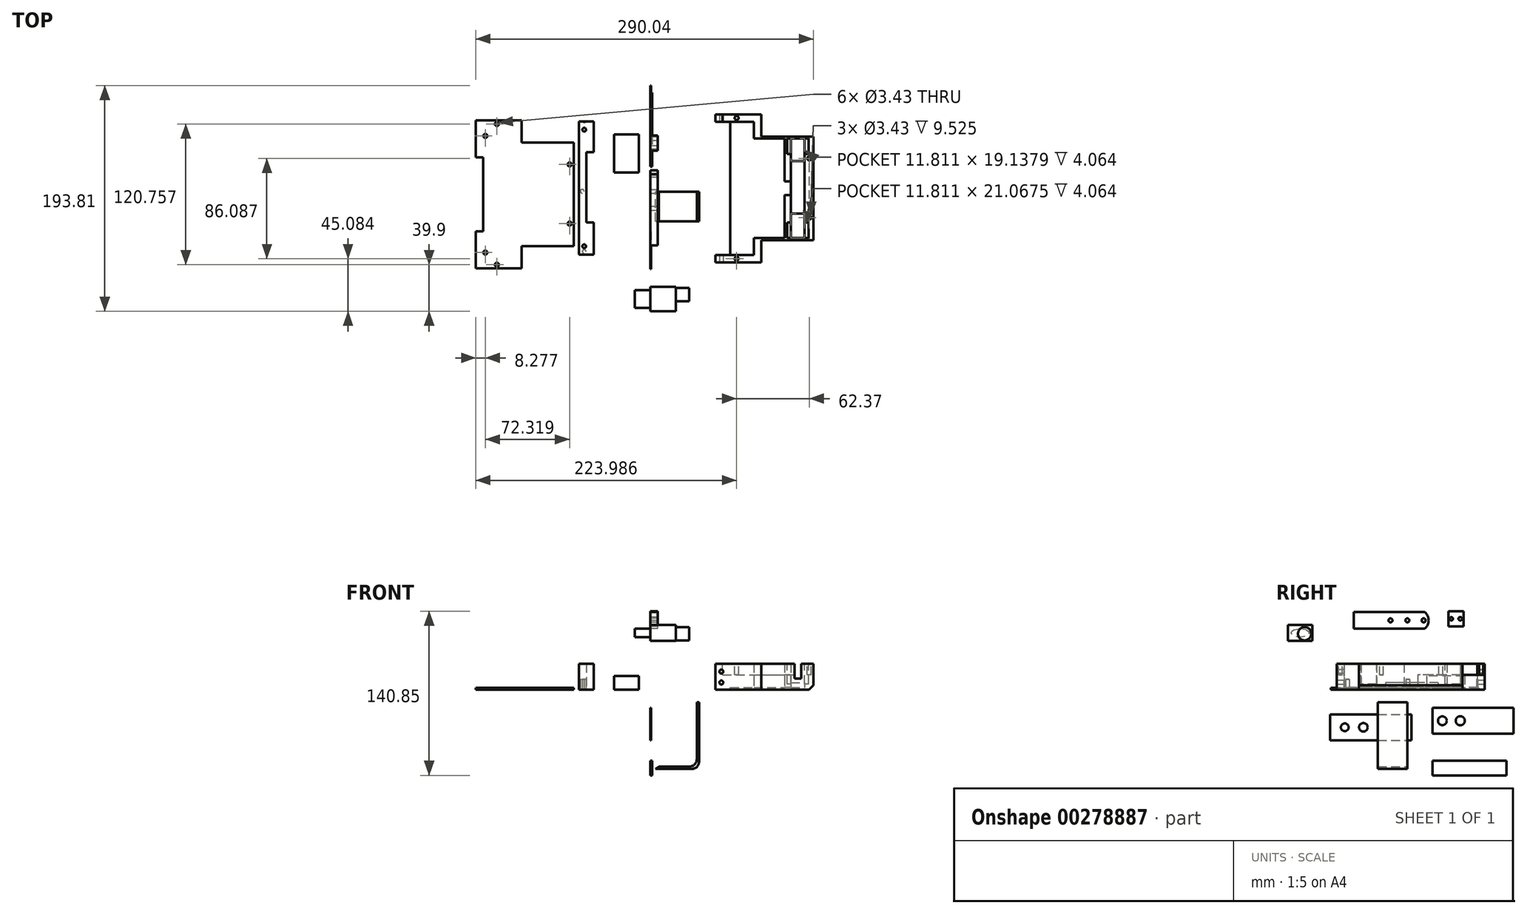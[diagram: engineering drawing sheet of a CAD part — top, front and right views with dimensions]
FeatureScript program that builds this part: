
annotation { "Feature Type Name" : "Feature", "Feature Type Description" : "" }
export const myFeature = defineFeature(function(context is Context, id is Id, definition is map)
    precondition{}
    {
        {
            var Q0;
            Q0=qCreatedBy(makeId("Top.planeOp"),FACE);
            var sketch = newSketch(context, id + "F0", { "sketchPlane" : qUnion([Q0])});
            skLineSegment(sketch, "E0.bottom", {"start": v(-61.13, 75.85) * mm, "end": v(-52.24, 75.85) * mm});
            skLineSegment(sketch, "E0.top", {"start": v(-61.13, -61.06) * mm, "end": v(-52.24, -61.06) * mm});
            skLineSegment(sketch, "E0.left", {"start": v(-61.13, 75.85) * mm, "end": v(-61.13, -61.06) * mm});
            skLineSegment(sketch, "E0.right", {"start": v(-48.43, 72.04) * mm, "end": v(-48.43, -57.25) * mm});
            skLineSegment(sketch, "E1.bottom", {"start": v(-48.43, -26.26) * mm, "end": v(-54.78, -26.26) * mm});
            skLineSegment(sketch, "E2", {"start": v(-48.43, 33.94) * mm, "end": v(-54.78, 33.94) * mm});
            skLineSegment(sketch, "E3", {"start": v(-54.78, 33.94) * mm, "end": v(-54.78, -26.26) * mm});
            skPoint(sketch, "E4.visualSharp", {"position": v(-48.43, 75.85) * mm});
            skArc(sketch, "E4.filletArc", {"start": v(-48.43, 72.04) * mm, "mid": v(-49.54, 74.73) * mm, "end": v(-52.24, 75.85) * mm});
            skPoint(sketch, "E5.visualSharp", {"position": v(-48.43, -61.06) * mm});
            skArc(sketch, "E5.filletArc", {"start": v(-52.24, -61.06) * mm, "mid": v(-49.54, -59.94) * mm, "end": v(-48.43, -57.25) * mm});
            skSolve(sketch);
        }
        {
            var Q0;
            {var subQ1=sQuery(id+"F0.wireOp",EDGE,"E0.bottom");Q0=makeQuery(id+"F0.imprint","IMPRINT",FACE,{"disambiguationData":[TD([[makeQuery(id+"F0.imprint","IMPRINT",EDGE,{"derivedFrom":subQ1}),-1.0]])]});}
            extrude(context, id + "F1", {"entities" : qUnion([Q0]), "depth" : 30.99 * mm});
        }
        {
            var Q0;
            Q0=makeQuery(id+"F1.opExtrude","CAP_FACE",FACE,{"disambiguationData":[OSD([sQuery(id+"F0.wireOp",EDGE,"E0.bottom"),sQuery(id+"F0.wireOp",EDGE,"E0.top"),sQuery(id+"F0.wireOp",EDGE,"E0.left"),sQuery(id+"F0.wireOp",EDGE,"E0.right"),sQuery(id+"F0.wireOp",EDGE,"E1.bottom"),sQuery(id+"F0.wireOp",EDGE,"E2"),sQuery(id+"F0.wireOp",EDGE,"E3"),sQuery(id+"F0.wireOp",EDGE,"E4.filletArc"),sQuery(id+"F0.wireOp",EDGE,"E5.filletArc")])],"isStart":false});
            var sketch = newSketch(context, id + "F2", { "sketchPlane" : qUnion([Q0])});
            skLineSegment(sketch, "E6", {"start": v(-56.68, -61.06) * mm, "end": v(-56.68, -46.84) * mm});
            skLineSegment(sketch, "E7", {"start": v(-56.68, 75.85) * mm, "end": v(-56.68, 53.24) * mm});
            skCircle(sketch, "E8", {"center": v(-56.68, 53.24) * mm, "radius": 1.59 * mm});
            skCircle(sketch, "E9", {"center": v(-56.68, -46.84) * mm, "radius": 1.59 * mm});
            skSolve(sketch);
        }
        {
            var Q0;
            Q0 = qSketchRegion(id + "F2", true);
            extrude(context, id + "F3", {"entities" : qUnion([Q0]), "operationType" : NewBodyOperationType.REMOVE, "oppositeDirection" : true, "depth" : 8.9 * mm});
        }
        {
            var Q0;
            Q0=makeQuery(id+"F1.opExtrude","CAP_FACE",FACE,{"disambiguationData":[OSD([sQuery(id+"F0.wireOp",EDGE,"E0.bottom"),sQuery(id+"F0.wireOp",EDGE,"E0.top"),sQuery(id+"F0.wireOp",EDGE,"E0.left"),sQuery(id+"F0.wireOp",EDGE,"E0.right"),sQuery(id+"F0.wireOp",EDGE,"E1.bottom"),sQuery(id+"F0.wireOp",EDGE,"E2"),sQuery(id+"F0.wireOp",EDGE,"E3"),sQuery(id+"F0.wireOp",EDGE,"E4.filletArc"),sQuery(id+"F0.wireOp",EDGE,"E5.filletArc")])],"isStart":true});
            var sketch = newSketch(context, id + "F4", { "sketchPlane" : qUnion([Q0])});
            skLineSegment(sketch, "E10", {"start": v(-56.68, 61.06) * mm, "end": v(-56.68, 51.4) * mm});
            skCircle(sketch, "E11", {"center": v(-56.68, 51.4) * mm, "radius": 1.59 * mm});
            skLineSegment(sketch, "E12", {"start": v(-58.44, 61.06) * mm, "end": v(-58.44, -0.4) * mm});
            skCircle(sketch, "E13", {"center": v(-58.44, -0.4) * mm, "radius": 1.59 * mm});
            skLineSegment(sketch, "E14", {"start": v(-56.68, -75.85) * mm, "end": v(-56.68, -60.86) * mm});
            skCircle(sketch, "E15", {"center": v(-56.68, -60.86) * mm, "radius": 1.59 * mm});
            skSolve(sketch);
        }
        {
            var Q0;
            Q0 = qSketchRegion(id + "F4", true);
            extrude(context, id + "F5", {"entities" : qUnion([Q0]), "operationType" : NewBodyOperationType.REMOVE, "oppositeDirection" : true, "depth" : 8.9 * mm});
        }
        {
            var Q0;
            Q0=qCreatedBy(makeId("Right.planeOp"),FACE);
            var sketch = newSketch(context, id + "F6", { "sketchPlane" : qUnion([Q0])});
            skLineSegment(sketch, "E16.bottom", {"start": v(-46.02, 52.32) * mm, "end": v(18.75, 52.32) * mm});
            skLineSegment(sketch, "E16.top", {"start": v(-46.02, 66.8) * mm, "end": v(18.75, 66.8) * mm});
            skLineSegment(sketch, "E16.left", {"start": v(-46.02, 52.32) * mm, "end": v(-46.02, 66.8) * mm});
            skLineSegment(sketch, "E16.right", {"start": v(18.75, 52.32) * mm, "end": v(18.75, 66.8) * mm});
            skArc(sketch, "E17", {"start": v(14.79, 52.32) * mm, "mid": v(18.28, 59.56) * mm, "end": v(14.79, 66.8) * mm});
            skSolve(sketch);
        }
        {
            var Q0;
            {var subQ0=sQuery(id+"F6.wireOp",EDGE,"E16.left");Q0=makeQuery(id+"F6.imprint","IMPRINT",FACE,{"disambiguationData":[TD([[makeQuery(id+"F6.imprint","IMPRINT",EDGE,{"derivedFrom":subQ0}),-1.0]])]});}
            extrude(context, id + "F7", {"entities" : qUnion([Q0]), "depth" : 6.35 * mm});
        }
        {
            var Q0;
            Q0=qCreatedBy(makeId("Right.planeOp"),FACE);
            var sketch = newSketch(context, id + "F8", { "sketchPlane" : qUnion([Q0])});
            skLineSegment(sketch, "E18.bottom", {"start": v(-66.47, -21.09) * mm, "end": v(3.63, -21.09) * mm});
            skLineSegment(sketch, "E18.top", {"start": v(-66.47, -43.31) * mm, "end": v(3.63, -43.31) * mm});
            skLineSegment(sketch, "E18.left", {"start": v(-66.47, -21.09) * mm, "end": v(-66.47, -43.31) * mm});
            skLineSegment(sketch, "E18.right", {"start": v(3.63, -21.09) * mm, "end": v(3.63, -43.31) * mm});
            skLineSegment(sketch, "E19", {"start": v(-66.47, -32.2) * mm, "end": v(-53.77, -32.2) * mm});
            skLineSegment(sketch, "E20", {"start": v(-53.77, -32.2) * mm, "end": v(-37.77, -32.2) * mm});
            skCircle(sketch, "E21", {"center": v(-53.77, -32.2) * mm, "radius": 3.3 * mm});
            skCircle(sketch, "E22", {"center": v(-37.77, -32.2) * mm, "radius": 3.68 * mm});
            skSolve(sketch);
        }
        {
            var Q0;
            Q0 = qSketchRegion(id + "F8", true);
            extrude(context, id + "F9", {"entities" : qUnion([Q0]), "depth" : 0.76 * mm});
        }
        {
            var Q0;
            Q0=qCreatedBy(makeId("Right.planeOp"),FACE);
            var sketch = newSketch(context, id + "F10", { "sketchPlane" : qUnion([Q0])});
            skLineSegment(sketch, "E23.bottom", {"start": v(21.66, -15.48) * mm, "end": v(91.25, -15.48) * mm});
            skLineSegment(sketch, "E23.top", {"start": v(21.66, -37.7) * mm, "end": v(91.25, -37.7) * mm});
            skLineSegment(sketch, "E23.left", {"start": v(21.66, -15.48) * mm, "end": v(21.66, -37.7) * mm});
            skLineSegment(sketch, "E23.right", {"start": v(91.25, -15.48) * mm, "end": v(91.25, -37.7) * mm});
            skLineSegment(sketch, "E24", {"start": v(30.04, -37.7) * mm, "end": v(30.04, -26.6) * mm});
            skLineSegment(sketch, "E25", {"start": v(30.04, -26.6) * mm, "end": v(21.66, -26.6) * mm});
            skLineSegment(sketch, "E26", {"start": v(21.66, -26.6) * mm, "end": v(30.04, -26.6) * mm});
            skCircle(sketch, "E27", {"center": v(30.04, -26.6) * mm, "radius": 3.78 * mm});
            skLineSegment(sketch, "E28", {"start": v(30.04, -26.6) * mm, "end": v(45.43, -26.6) * mm});
            skCircle(sketch, "E29", {"center": v(45.43, -26.6) * mm, "radius": 3.84 * mm});
            skPoint(sketch, "E30", {"position": v(21.66, -26.6) * mm});
            skSolve(sketch);
        }
        {
            var Q0;
            Q0 = qSketchRegion(id + "F10", true);
            extrude(context, id + "F11", {"entities" : qUnion([Q0]), "depth" : 0.76 * mm});
        }
        {
            var Q0;
            Q0=makeQuery(id+"F7.opExtrude","CAP_FACE",FACE,{"disambiguationData":[OSD([sQuery(id+"F6.wireOp",EDGE,"E16.bottom"),sQuery(id+"F6.wireOp",EDGE,"E16.top"),sQuery(id+"F6.wireOp",EDGE,"E16.left"),sQuery(id+"F6.wireOp",EDGE,"E17")])],"isStart":true});
            var sketch = newSketch(context, id + "F12", { "sketchPlane" : qUnion([Q0])});
            skCircle(sketch, "E31", {"center": v(0, 59.56) * mm, "radius": 1.71 * mm});
            skLineSegment(sketch, "E32", {"start": v(0, 59.56) * mm, "end": v(14.48, 59.56) * mm});
            skCircle(sketch, "E33", {"center": v(14.48, 59.56) * mm, "radius": 1.71 * mm});
            skLineSegment(sketch, "E34", {"start": v(-18.28, 59.56) * mm, "end": v(-13.96, 59.56) * mm});
            skCircle(sketch, "E35", {"center": v(-13.96, 59.56) * mm, "radius": 1.73 * mm});
            skPoint(sketch, "E36", {"position": v(-18.28, 59.56) * mm});
            skSolve(sketch);
        }
        {
            var Q0;
            Q0 = qSketchRegion(id + "F12", true);
            extrude(context, id + "F13", {"entities" : qUnion([Q0]), "operationType" : NewBodyOperationType.REMOVE, "endBound" : BoundingType.THROUGH_ALL, "oppositeDirection" : true, "depth" : 25.4 * mm});
        }
        {
            var Q0;
            Q0=qCreatedBy(makeId("Top.planeOp"),FACE);
            var sketch = newSketch(context, id + "F14", { "sketchPlane" : qUnion([Q0])});
            skLineSegment(sketch, "E37.bottom", {"start": v(-9.82, 49.07) * mm, "end": v(-31.15, 49.07) * mm});
            skLineSegment(sketch, "E37.top", {"start": v(-9.82, 16.56) * mm, "end": v(-31.15, 16.56) * mm});
            skLineSegment(sketch, "E37.left", {"start": v(-9.82, 49.07) * mm, "end": v(-9.82, 16.56) * mm});
            skLineSegment(sketch, "E37.right", {"start": v(-31.15, 49.07) * mm, "end": v(-31.15, 16.56) * mm});
            skSolve(sketch);
        }
        {
            var Q0;
            Q0 = qSketchRegion(id + "F14", true);
            extrude(context, id + "F15", {"entities" : qUnion([Q0]), "depth" : 11.94 * mm});
        }
        {
            var Q0;
            Q0=qCreatedBy(makeId("Top.planeOp"),FACE);
            var sketch = newSketch(context, id + "F16", { "sketchPlane" : qUnion([Q0])});
            skLineSegment(sketch, "E38.left", {"start": v(55.93, 66.44) * mm, "end": v(55.93, -60.56) * mm});
            skLineSegment(sketch, "E39.top", {"start": v(95.3, 47.4) * mm, "end": v(140.19, 47.4) * mm});
            skLineSegment(sketch, "E40", {"start": v(55.93, 2.94) * mm, "end": v(70.8, 2.94) * mm});
            skLineSegment(sketch, "E41.MirrorCS", {"start": v(95.3, -41.5) * mm, "end": v(140.19, -41.5) * mm});
            skLineSegment(sketch, "E42", {"start": v(55.93, -60.56) * mm, "end": v(95.3, -60.56) * mm});
            skLineSegment(sketch, "E43", {"start": v(95.3, -60.56) * mm, "end": v(95.3, -41.5) * mm});
            skLineSegment(sketch, "E44", {"start": v(55.93, 66.44) * mm, "end": v(95.3, 66.44) * mm});
            skLineSegment(sketch, "E45", {"start": v(95.3, 66.44) * mm, "end": v(95.3, 47.4) * mm});
            skLineSegment(sketch, "E46", {"start": v(140.19, 47.4) * mm, "end": v(140.19, -41.5) * mm});
            skSolve(sketch);
        }
        {
            var Q0;
            Q0 = qSketchRegion(id + "F16", true);
            extrude(context, id + "F17", {"entities" : qUnion([Q0]), "depth" : 1.9 * mm});
        }
        {
            var Q0;
            Q0=makeQuery(id+"F17.opExtrude","CAP_FACE",FACE,{"disambiguationData":[OSD([sQuery(id+"F16.wireOp",EDGE,"E38.left"),sQuery(id+"F16.wireOp",EDGE,"E39.top"),sQuery(id+"F16.wireOp",EDGE,"E41.MirrorCS"),sQuery(id+"F16.wireOp",EDGE,"E42"),sQuery(id+"F16.wireOp",EDGE,"E43"),sQuery(id+"F16.wireOp",EDGE,"E44"),sQuery(id+"F16.wireOp",EDGE,"E45"),sQuery(id+"F16.wireOp",EDGE,"E46")])],"isStart":false});
            var sketch = newSketch(context, id + "F18", { "sketchPlane" : qUnion([Q0])});
            skLineSegment(sketch, "E47.left", {"start": v(55.93, 66.44) * mm, "end": v(55.93, -60.56) * mm});
            skLineSegment(sketch, "E48.top", {"start": v(95.3, 47.4) * mm, "end": v(140.19, 47.4) * mm});
            skLineSegment(sketch, "E49", {"start": v(55.93, 2.94) * mm, "end": v(68.63, 2.94) * mm});
            skLineSegment(sketch, "E50.MirrorCS", {"start": v(95.3, -41.5) * mm, "end": v(140.19, -41.5) * mm});
            skLineSegment(sketch, "E51", {"start": v(55.93, -60.56) * mm, "end": v(95.3, -60.56) * mm});
            skLineSegment(sketch, "E52", {"start": v(95.3, -60.56) * mm, "end": v(95.3, -41.5) * mm});
            skLineSegment(sketch, "E53", {"start": v(55.93, 66.44) * mm, "end": v(95.3, 66.44) * mm});
            skLineSegment(sketch, "E54", {"start": v(95.3, 66.44) * mm, "end": v(95.3, 47.4) * mm});
            skLineSegment(sketch, "E55", {"start": v(140.19, 47.4) * mm, "end": v(140.19, -41.5) * mm});
            skLineSegment(sketch, "E56.0", {"start": v(133.84, 45.62) * mm, "end": v(133.84, -39.73) * mm});
            skLineSegment(sketch, "E57.0", {"start": v(88.95, 45.62) * mm, "end": v(133.84, 45.62) * mm});
            skLineSegment(sketch, "E58.0", {"start": v(88.95, -39.73) * mm, "end": v(133.84, -39.73) * mm});
            skLineSegment(sketch, "E59.0", {"start": v(88.95, 60.1) * mm, "end": v(88.95, 45.62) * mm});
            skLineSegment(sketch, "E59.1", {"start": v(88.95, -54.2) * mm, "end": v(88.95, -39.73) * mm});
            skLineSegment(sketch, "E59.2", {"start": v(68.63, -54.2) * mm, "end": v(88.95, -54.2) * mm});
            skLineSegment(sketch, "E59.4", {"start": v(68.63, 60.1) * mm, "end": v(88.95, 60.1) * mm});
            skLineSegment(sketch, "E60", {"start": v(68.63, 60.1) * mm, "end": v(68.63, -54.2) * mm});
            skLineSegment(sketch, "E61.bottom", {"start": v(62.73, 27.73) * mm, "end": v(49.13, 27.73) * mm});
            skLineSegment(sketch, "E61.top", {"start": v(62.73, -21.84) * mm, "end": v(49.13, -21.84) * mm});
            skLineSegment(sketch, "E61.left", {"start": v(62.73, 27.73) * mm, "end": v(62.73, -21.84) * mm});
            skLineSegment(sketch, "E61.right", {"start": v(49.13, 27.73) * mm, "end": v(49.13, -21.84) * mm});
            skPoint(sketch, "E61.middle", {"position": v(55.93, 2.94) * mm});
            skSolve(sketch);
        }
        {
            var Q0;
            Q0=makeQuery(id+"F18.imprint","IMPRINT",FACE,{"disambiguationData":[TD([[makeQuery(id+"F18.imprint","IMPRINT",EDGE,{"derivedFrom":sQuery(id+"F18.wireOp",EDGE,"E48.top")}),-1.0]])]});
            extrude(context, id + "F19", {"entities" : qUnion([Q0]), "operationType" : NewBodyOperationType.ADD, "depth" : 20.32 * mm});
        }
        {
            var Q0;
            Q0=qCreatedBy(makeId("Right.planeOp"),FACE);
            var sketch = newSketch(context, id + "F20", { "sketchPlane" : qUnion([Q0])});
            skLineSegment(sketch, "E62.bottom", {"start": v(-81.73, 55.57) * mm, "end": v(-102.56, 55.57) * mm});
            skLineSegment(sketch, "E62.top", {"start": v(-81.73, 42.11) * mm, "end": v(-102.56, 42.11) * mm});
            skLineSegment(sketch, "E62.left", {"start": v(-81.73, 55.57) * mm, "end": v(-81.73, 42.11) * mm});
            skLineSegment(sketch, "E62.right", {"start": v(-102.56, 55.57) * mm, "end": v(-102.56, 42.11) * mm});
            skPoint(sketch, "E62.middle", {"position": v(-92.15, 48.84) * mm});
            skSolve(sketch);
        }
        {
            var Q0;
            Q0 = qSketchRegion(id + "F20", true);
            extrude(context, id + "F21", {"entities" : qUnion([Q0]), "depth" : 21.84 * mm});
        }
        {
            var Q0;
            Q0=makeQuery(id+"F21.opExtrude","CAP_FACE",FACE,{"disambiguationData":[OSD([sQuery(id+"F20.wireOp",EDGE,"E62.bottom"),sQuery(id+"F20.wireOp",EDGE,"E62.top"),sQuery(id+"F20.wireOp",EDGE,"E62.left"),sQuery(id+"F20.wireOp",EDGE,"E62.right")])],"isStart":false});
            var sketch = newSketch(context, id + "F22", { "sketchPlane" : qUnion([Q0])});
            skCircle(sketch, "E63", {"center": v(-88.2, 48.13) * mm, "radius": 5.72 * mm});
            skSolve(sketch);
        }
        {
            var Q0;
            Q0 = qSketchRegion(id + "F22", true);
            extrude(context, id + "F23", {"entities" : qUnion([Q0]), "operationType" : NewBodyOperationType.ADD, "depth" : 11.68 * mm});
        }
        {
            var Q0;
            Q0=makeQuery(id+"F21.opExtrude","CAP_FACE",FACE,{"disambiguationData":[OSD([sQuery(id+"F20.wireOp",EDGE,"E62.bottom"),sQuery(id+"F20.wireOp",EDGE,"E62.top"),sQuery(id+"F20.wireOp",EDGE,"E62.left"),sQuery(id+"F20.wireOp",EDGE,"E62.right")])],"isStart":true});
            var sketch = newSketch(context, id + "F24", { "sketchPlane" : qUnion([Q0])});
            skEllipse(sketch, "E64", {"center": v(92.15, 48.84) * mm, "majorRadius": 7.65 * mm, "minorRadius": 3.54 * mm, "majorAxis": v(1, 0)});
            skPoint(sketch, "E64.centerSnap0", {"position": v(92.15, 55.57) * mm});
            skPoint(sketch, "E64.centerSnap1", {"position": v(81.73, 48.84) * mm});
            skSolve(sketch);
        }
        {
            var Q0;
            Q0 = qSketchRegion(id + "F24", true);
            extrude(context, id + "F25", {"entities" : qUnion([Q0]), "operationType" : NewBodyOperationType.ADD, "depth" : 13.2 * mm});
        }
        {
            var Q0;
            Q0=qCreatedBy(makeId("Right.planeOp"),FACE);
            var sketch = newSketch(context, id + "F26", { "sketchPlane" : qUnion([Q0])});
            skLineSegment(sketch, "E65.bottom", {"start": v(48.2, 67.4) * mm, "end": v(35.25, 67.4) * mm});
            skLineSegment(sketch, "E65.top", {"start": v(48.2, 54.44) * mm, "end": v(35.25, 54.44) * mm});
            skLineSegment(sketch, "E65.left", {"start": v(48.2, 67.4) * mm, "end": v(48.2, 54.44) * mm});
            skLineSegment(sketch, "E65.right", {"start": v(35.25, 67.4) * mm, "end": v(35.25, 54.44) * mm});
            skPoint(sketch, "E65.middle", {"position": v(41.73, 60.92) * mm});
            skCircle(sketch, "E66", {"center": v(37.83, 60.92) * mm, "radius": 1.38 * mm});
            skCircle(sketch, "E67", {"center": v(45.4, 60.92) * mm, "radius": 1.5 * mm});
            skSolve(sketch);
        }
        {
            var Q0;
            Q0 = qSketchRegion(id + "F26", true);
            extrude(context, id + "F27", {"entities" : qUnion([Q0]), "depth" : 6.35 * mm});
        }
        {
            var Q0;
            Q0=makeQuery(id+"F17.opExtrude","CAP_EDGE",EDGE,{"disambiguationData":[OSD([sQuery(id+"F16.wireOp",EDGE,"E46")])],"isStart":true});
            chamfer(context, id + "F28", {"entities" : qUnion([Q0]), "width" : 3.8 * mm, "tangentPropagation" : true});
        }
        {
            var Q0;
            Q0=makeQuery(id+"F19.boolean.opBoolean","SPLIT",FACE,{"disambiguationData":[TD([makeQuery(id+"F19.opExtrude","SWEPT_FACE",FACE,{"disambiguationData":[OSD([sQuery(id+"F18.wireOp",EDGE,"E56.0")])]})])],"derivedFrom":makeQuery(id+"F17.opExtrude","CAP_FACE",FACE,{"disambiguationData":[OSD([sQuery(id+"F16.wireOp",EDGE,"E38.left"),sQuery(id+"F16.wireOp",EDGE,"E39.top"),sQuery(id+"F16.wireOp",EDGE,"E41.MirrorCS"),sQuery(id+"F16.wireOp",EDGE,"E42"),sQuery(id+"F16.wireOp",EDGE,"E43"),sQuery(id+"F16.wireOp",EDGE,"E44"),sQuery(id+"F16.wireOp",EDGE,"E45"),sQuery(id+"F16.wireOp",EDGE,"E46")])],"isStart":false})});
            var sketch = newSketch(context, id + "F29", { "sketchPlane" : qUnion([Q0])});
            skLineSegment(sketch, "E68.bottom", {"start": v(133.84, 45.62) * mm, "end": v(132.57, 45.62) * mm});
            skLineSegment(sketch, "E68.top", {"start": v(133.84, -39.73) * mm, "end": v(132.57, -39.73) * mm});
            skLineSegment(sketch, "E68.left", {"start": v(133.84, 45.62) * mm, "end": v(133.84, -39.73) * mm});
            skLineSegment(sketch, "E68.right", {"start": v(132.57, 45.62) * mm, "end": v(132.57, -39.73) * mm});
            skLineSegment(sketch, "E69", {"start": v(132.57, 35.44) * mm, "end": v(120.76, 35.44) * mm});
            skLineSegment(sketch, "E70.bottom", {"start": v(120.76, 45.62) * mm, "end": v(115.25, 45.62) * mm});
            skLineSegment(sketch, "E70.top", {"start": v(120.76, 8.85) * mm, "end": v(115.25, 8.85) * mm});
            skLineSegment(sketch, "E70.left", {"start": v(120.76, 45.62) * mm, "end": v(120.76, 8.85) * mm});
            skLineSegment(sketch, "E70.right", {"start": v(115.25, 45.62) * mm, "end": v(115.25, 8.85) * mm});
            skLineSegment(sketch, "E71", {"start": v(133.84, 2.94) * mm, "end": v(125.96, 2.94) * mm});
            skLineSegment(sketch, "E72.MirrorCS", {"start": v(120.76, -39.73) * mm, "end": v(115.25, -39.73) * mm});
            skLineSegment(sketch, "E73.MirrorCS", {"start": v(120.76, -2.96) * mm, "end": v(115.25, -2.96) * mm});
            skLineSegment(sketch, "E74.MirrorCS", {"start": v(120.76, -39.73) * mm, "end": v(120.76, -2.96) * mm});
            skLineSegment(sketch, "E75.MirrorCS", {"start": v(115.25, -39.73) * mm, "end": v(115.25, -2.96) * mm});
            skSolve(sketch);
        }
        {
            var Q0;
            Q0 = qSketchRegion(id + "F29", true);
            var Q1;
            Q1=makeQuery(id+"F19.opExtrude","CAP_FACE",FACE,{"disambiguationData":[OSD([sQuery(id+"F18.wireOp",EDGE,"E47.left"),sQuery(id+"F18.wireOp",EDGE,"E48.top"),sQuery(id+"F18.wireOp",EDGE,"E50.MirrorCS"),sQuery(id+"F18.wireOp",EDGE,"E51"),sQuery(id+"F18.wireOp",EDGE,"E52"),sQuery(id+"F18.wireOp",EDGE,"E53"),sQuery(id+"F18.wireOp",EDGE,"E54"),sQuery(id+"F18.wireOp",EDGE,"E55"),sQuery(id+"F18.wireOp",EDGE,"E56.0"),sQuery(id+"F18.wireOp",EDGE,"E57.0"),sQuery(id+"F18.wireOp",EDGE,"E58.0"),sQuery(id+"F18.wireOp",EDGE,"E59.0"),sQuery(id+"F18.wireOp",EDGE,"E59.1"),sQuery(id+"F18.wireOp",EDGE,"E59.2"),sQuery(id+"F18.wireOp",EDGE,"E59.4"),sQuery(id+"F18.wireOp",EDGE,"E60"),sQuery(id+"F18.wireOp",EDGE,"E61.bottom"),sQuery(id+"F18.wireOp",EDGE,"E61.top"),sQuery(id+"F18.wireOp",EDGE,"E61.left")])],"isStart":false});
            extrude(context, id + "F30", {"entities" : qUnion([Q0]), "operationType" : NewBodyOperationType.ADD, "endBound" : BoundingType.UP_TO_SURFACE, "endBoundEntityFace" : qUnion([Q1]), "depth" : 22.22 * mm});
        }
        {
            var Q0;
            Q0=makeQuery(id+"F34.boolean.opBoolean","MERGE",FACE,{"derivedFrom":[makeQuery(id+"F19.boolean.opBoolean","SPLIT",FACE,{"disambiguationData":[TD([makeQuery(id+"F19.opExtrude","SWEPT_FACE",FACE,{"disambiguationData":[OSD([sQuery(id+"F18.wireOp",EDGE,"E56.0")])]})])],"derivedFrom":makeQuery(id+"F17.opExtrude","CAP_FACE",FACE,{"disambiguationData":[OSD([sQuery(id+"F16.wireOp",EDGE,"E38.left"),sQuery(id+"F16.wireOp",EDGE,"E39.top"),sQuery(id+"F16.wireOp",EDGE,"E41.MirrorCS"),sQuery(id+"F16.wireOp",EDGE,"E42"),sQuery(id+"F16.wireOp",EDGE,"E43"),sQuery(id+"F16.wireOp",EDGE,"E44"),sQuery(id+"F16.wireOp",EDGE,"E45"),sQuery(id+"F16.wireOp",EDGE,"E46")])],"isStart":false})}),makeQuery(id+"F34.opExtrude","CAP_FACE",FACE,{"disambiguationData":[OSD([sQuery(id+"F33.wireOp",EDGE,"E77.bottom"),sQuery(id+"F33.wireOp",EDGE,"E77.top"),sQuery(id+"F33.wireOp",EDGE,"E77.left"),sQuery(id+"F33.wireOp",EDGE,"E77.right")])],"isStart":false}),makeQuery(id+"F34.opExtrude","CAP_FACE",FACE,{"disambiguationData":[OSD([sQuery(id+"F33.wireOp",EDGE,"E81.MirrorCS"),sQuery(id+"F33.wireOp",EDGE,"E82.MirrorCS"),sQuery(id+"F33.wireOp",EDGE,"E83.MirrorCS"),sQuery(id+"F33.wireOp",EDGE,"E84.MirrorCS")])],"isStart":false})]});
            var sketch = newSketch(context, id + "F31", { "sketchPlane" : qUnion([Q0])});
            skLineSegment(sketch, "E76.bottom", {"start": v(120.76, 26.48) * mm, "end": v(132.57, 26.48) * mm});
            skLineSegment(sketch, "E76.top", {"start": v(120.76, -18.66) * mm, "end": v(132.57, -18.66) * mm});
            skLineSegment(sketch, "E76.left", {"start": v(120.76, 26.48) * mm, "end": v(120.76, -18.66) * mm});
            skLineSegment(sketch, "E76.right", {"start": v(132.57, 26.48) * mm, "end": v(132.57, -18.66) * mm});
            skSolve(sketch);
        }
        {
            var Q0;
            Q0 = qSketchRegion(id + "F31", true);
            extrude(context, id + "F32", {"entities" : qUnion([Q0]), "operationType" : NewBodyOperationType.ADD, "depth" : 4.06 * mm});
        }
        {
            var Q0;
            Q0=makeQuery(id+"F30.boolean.opBoolean","MERGE",FACE,{"derivedFrom":[makeQuery(id+"F19.opExtrude","CAP_FACE",FACE,{"disambiguationData":[OSD([sQuery(id+"F18.wireOp",EDGE,"E47.left"),sQuery(id+"F18.wireOp",EDGE,"E48.top"),sQuery(id+"F18.wireOp",EDGE,"E50.MirrorCS"),sQuery(id+"F18.wireOp",EDGE,"E51"),sQuery(id+"F18.wireOp",EDGE,"E52"),sQuery(id+"F18.wireOp",EDGE,"E53"),sQuery(id+"F18.wireOp",EDGE,"E54"),sQuery(id+"F18.wireOp",EDGE,"E55"),sQuery(id+"F18.wireOp",EDGE,"E56.0"),sQuery(id+"F18.wireOp",EDGE,"E57.0"),sQuery(id+"F18.wireOp",EDGE,"E58.0"),sQuery(id+"F18.wireOp",EDGE,"E59.0"),sQuery(id+"F18.wireOp",EDGE,"E59.1"),sQuery(id+"F18.wireOp",EDGE,"E59.2"),sQuery(id+"F18.wireOp",EDGE,"E59.4"),sQuery(id+"F18.wireOp",EDGE,"E60"),sQuery(id+"F18.wireOp",EDGE,"E61.bottom"),sQuery(id+"F18.wireOp",EDGE,"E61.top"),sQuery(id+"F18.wireOp",EDGE,"E61.left")])],"isStart":false}),makeQuery(id+"F30.opExtrude","CAP_FACE",FACE,{"disambiguationData":[OSD([sQuery(id+"F29.wireOp",EDGE,"E68.bottom"),sQuery(id+"F29.wireOp",EDGE,"E68.top"),sQuery(id+"F29.wireOp",EDGE,"E68.left"),sQuery(id+"F29.wireOp",EDGE,"E68.right")])],"isStart":false}),makeQuery(id+"F30.opExtrude","CAP_FACE",FACE,{"disambiguationData":[OSD([sQuery(id+"F29.wireOp",EDGE,"E70.bottom"),sQuery(id+"F29.wireOp",EDGE,"E70.top"),sQuery(id+"F29.wireOp",EDGE,"E70.left"),sQuery(id+"F29.wireOp",EDGE,"E70.right")])],"isStart":false}),makeQuery(id+"F30.opExtrude","CAP_FACE",FACE,{"disambiguationData":[OSD([sQuery(id+"F29.wireOp",EDGE,"E72.MirrorCS"),sQuery(id+"F29.wireOp",EDGE,"E73.MirrorCS"),sQuery(id+"F29.wireOp",EDGE,"E74.MirrorCS"),sQuery(id+"F29.wireOp",EDGE,"E75.MirrorCS")])],"isStart":false})]});
            var sketch = newSketch(context, id + "F33", { "sketchPlane" : qUnion([Q0])});
            skLineSegment(sketch, "E77.bottom", {"start": v(135.87, 45.62) * mm, "end": v(117.56, 45.62) * mm});
            skLineSegment(sketch, "E77.top", {"start": v(135.87, 32.28) * mm, "end": v(117.56, 32.28) * mm});
            skLineSegment(sketch, "E77.left", {"start": v(135.87, 45.62) * mm, "end": v(135.87, 32.28) * mm});
            skLineSegment(sketch, "E77.right", {"start": v(117.56, 45.62) * mm, "end": v(117.56, 32.28) * mm});
            skPoint(sketch, "E77.middle", {"position": v(126.71, 38.95) * mm});
            skPoint(sketch, "E77.middle.positionSnap0", {"position": v(126.71, 45.62) * mm});
            skPoint(sketch, "E77.centerSnap0", {"position": v(126.66, 45.62) * mm});
            skLineSegment(sketch, "E78", {"start": v(132.57, 2.94) * mm, "end": v(125.45, 2.94) * mm});
            skPoint(sketch, "E79.MirrorP", {"position": v(126.71, -39.73) * mm});
            skPoint(sketch, "E80.MirrorP", {"position": v(126.66, -39.73) * mm});
            skLineSegment(sketch, "E81.MirrorCS", {"start": v(135.87, -39.73) * mm, "end": v(117.56, -39.73) * mm});
            skLineSegment(sketch, "E82.MirrorCS", {"start": v(135.87, -26.4) * mm, "end": v(117.56, -26.4) * mm});
            skLineSegment(sketch, "E83.MirrorCS", {"start": v(135.87, -39.73) * mm, "end": v(135.87, -26.4) * mm});
            skLineSegment(sketch, "E84.MirrorCS", {"start": v(117.56, -39.73) * mm, "end": v(117.56, -26.4) * mm});
            skPoint(sketch, "E85.MirrorP", {"position": v(126.71, -33.06) * mm});
            skSolve(sketch);
        }
        {
            var Q0;
            Q0 = qSketchRegion(id + "F33", true);
            var Q1;
            Q1=makeQuery(id+"F19.boolean.opBoolean","SPLIT",FACE,{"disambiguationData":[TD([makeQuery(id+"F19.opExtrude","SWEPT_FACE",FACE,{"disambiguationData":[OSD([sQuery(id+"F18.wireOp",EDGE,"E56.0")])]})])],"derivedFrom":makeQuery(id+"F17.opExtrude","CAP_FACE",FACE,{"disambiguationData":[OSD([sQuery(id+"F16.wireOp",EDGE,"E38.left"),sQuery(id+"F16.wireOp",EDGE,"E39.top"),sQuery(id+"F16.wireOp",EDGE,"E41.MirrorCS"),sQuery(id+"F16.wireOp",EDGE,"E42"),sQuery(id+"F16.wireOp",EDGE,"E43"),sQuery(id+"F16.wireOp",EDGE,"E44"),sQuery(id+"F16.wireOp",EDGE,"E45"),sQuery(id+"F16.wireOp",EDGE,"E46")])],"isStart":false})});
            extrude(context, id + "F34", {"entities" : qUnion([Q0]), "operationType" : NewBodyOperationType.REMOVE, "endBound" : BoundingType.SYMMETRIC, "oppositeDirection" : true, "endBoundEntityFace" : qUnion([Q1]), "depth" : 34.54 * mm});
        }
        {
            var Q0;
            Q0=makeQuery(id+"F30.boolean.opBoolean","MERGE",FACE,{"derivedFrom":[makeQuery(id+"F19.opExtrude","CAP_FACE",FACE,{"disambiguationData":[OSD([sQuery(id+"F18.wireOp",EDGE,"E47.left"),sQuery(id+"F18.wireOp",EDGE,"E48.top"),sQuery(id+"F18.wireOp",EDGE,"E50.MirrorCS"),sQuery(id+"F18.wireOp",EDGE,"E51"),sQuery(id+"F18.wireOp",EDGE,"E52"),sQuery(id+"F18.wireOp",EDGE,"E53"),sQuery(id+"F18.wireOp",EDGE,"E54"),sQuery(id+"F18.wireOp",EDGE,"E55"),sQuery(id+"F18.wireOp",EDGE,"E56.0"),sQuery(id+"F18.wireOp",EDGE,"E57.0"),sQuery(id+"F18.wireOp",EDGE,"E58.0"),sQuery(id+"F18.wireOp",EDGE,"E59.0"),sQuery(id+"F18.wireOp",EDGE,"E59.1"),sQuery(id+"F18.wireOp",EDGE,"E59.2"),sQuery(id+"F18.wireOp",EDGE,"E59.4"),sQuery(id+"F18.wireOp",EDGE,"E60"),sQuery(id+"F18.wireOp",EDGE,"E61.bottom"),sQuery(id+"F18.wireOp",EDGE,"E61.top"),sQuery(id+"F18.wireOp",EDGE,"E61.left")])],"isStart":false}),makeQuery(id+"F30.opExtrude","CAP_FACE",FACE,{"disambiguationData":[OSD([sQuery(id+"F29.wireOp",EDGE,"E68.bottom"),sQuery(id+"F29.wireOp",EDGE,"E68.top"),sQuery(id+"F29.wireOp",EDGE,"E68.left"),sQuery(id+"F29.wireOp",EDGE,"E68.right")])],"isStart":false}),makeQuery(id+"F30.opExtrude","CAP_FACE",FACE,{"disambiguationData":[OSD([sQuery(id+"F29.wireOp",EDGE,"E70.bottom"),sQuery(id+"F29.wireOp",EDGE,"E70.top"),sQuery(id+"F29.wireOp",EDGE,"E70.left"),sQuery(id+"F29.wireOp",EDGE,"E70.right")])],"isStart":false}),makeQuery(id+"F30.opExtrude","CAP_FACE",FACE,{"disambiguationData":[OSD([sQuery(id+"F29.wireOp",EDGE,"E72.MirrorCS"),sQuery(id+"F29.wireOp",EDGE,"E73.MirrorCS"),sQuery(id+"F29.wireOp",EDGE,"E74.MirrorCS"),sQuery(id+"F29.wireOp",EDGE,"E75.MirrorCS")])],"isStart":false})]});
            var sketch = newSketch(context, id + "F35", { "sketchPlane" : qUnion([Q0])});
            skLineSegment(sketch, "E86.bottom", {"start": v(129.5, 47.4) * mm, "end": v(123.93, 47.4) * mm});
            skLineSegment(sketch, "E86.top", {"start": v(129.5, 43.84) * mm, "end": v(123.93, 43.84) * mm});
            skLineSegment(sketch, "E86.left", {"start": v(129.5, 47.4) * mm, "end": v(129.5, 43.84) * mm});
            skLineSegment(sketch, "E86.right", {"start": v(123.93, 47.4) * mm, "end": v(123.93, 43.84) * mm});
            skPoint(sketch, "E86.middle", {"position": v(126.71, 45.62) * mm});
            skLineSegment(sketch, "E87", {"start": v(140.2, 2.94) * mm, "end": v(140.19, 2.94) * mm});
            skPoint(sketch, "E87.endSnap0", {"position": v(132.57, 2.94) * mm});
            skPoint(sketch, "E88.MirrorP", {"position": v(126.71, -39.73) * mm});
            skLineSegment(sketch, "E89.MirrorCS", {"start": v(129.5, -41.5) * mm, "end": v(123.93, -41.5) * mm});
            skLineSegment(sketch, "E90.MirrorCS", {"start": v(129.5, -37.95) * mm, "end": v(123.93, -37.95) * mm});
            skLineSegment(sketch, "E91.MirrorCS", {"start": v(129.5, -41.5) * mm, "end": v(129.5, -37.95) * mm});
            skLineSegment(sketch, "E92.MirrorCS", {"start": v(123.93, -41.5) * mm, "end": v(123.93, -37.95) * mm});
            skSolve(sketch);
        }
        {
            var Q0;
            Q0 = qSketchRegion(id + "F35", true);
            extrude(context, id + "F36", {"entities" : qUnion([Q0]), "operationType" : NewBodyOperationType.REMOVE, "oppositeDirection" : true, "depth" : 12.7 * mm});
        }
        {
            var Q0;
            {var subQ3=sQuery(id+"F16.wireOp",EDGE,"E38.left");Q0=makeQuery(id+"F19.boolean.opBoolean","SPLIT",FACE,{"disambiguationData":[TD([makeQuery(id+"F17.opExtrude","SWEPT_FACE",FACE,{"disambiguationData":[OSD([subQ3])]})])],"derivedFrom":makeQuery(id+"F17.opExtrude","CAP_FACE",FACE,{"disambiguationData":[OSD([subQ3,sQuery(id+"F16.wireOp",EDGE,"E39.top"),sQuery(id+"F16.wireOp",EDGE,"E41.MirrorCS"),sQuery(id+"F16.wireOp",EDGE,"E42"),sQuery(id+"F16.wireOp",EDGE,"E43"),sQuery(id+"F16.wireOp",EDGE,"E44"),sQuery(id+"F16.wireOp",EDGE,"E45"),sQuery(id+"F16.wireOp",EDGE,"E46")])],"isStart":false})});}
            var sketch = newSketch(context, id + "F37", { "sketchPlane" : qUnion([Q0])});
            skLineSegment(sketch, "E93.bottom", {"start": v(62.73, 27.73) * mm, "end": v(55.93, 27.73) * mm});
            skLineSegment(sketch, "E93.top", {"start": v(62.73, -21.84) * mm, "end": v(55.93, -21.84) * mm});
            skLineSegment(sketch, "E93.left", {"start": v(62.73, 27.73) * mm, "end": v(62.73, -21.84) * mm});
            skLineSegment(sketch, "E93.right", {"start": v(55.93, 27.73) * mm, "end": v(55.93, -21.84) * mm});
            skSolve(sketch);
        }
        {
            var Q0;
            Q0 = qSketchRegion(id + "F37", true);
            extrude(context, id + "F38", {"entities" : qUnion([Q0]), "operationType" : NewBodyOperationType.REMOVE, "oppositeDirection" : true, "depth" : 25.4 * mm});
        }
        {
            var Q0;
            Q0=qCreatedBy(makeId("Front.planeOp"),FACE);
            var sketch = newSketch(context, id + "F39", { "sketchPlane" : qUnion([Q0])});
            skLineSegment(sketch, "E94", {"start": v(41.94, -10.83) * mm, "end": v(41.94, -61.63) * mm});
            skLineSegment(sketch, "E95", {"start": v(35.6, -67.98) * mm, "end": v(7.4, -67.98) * mm});
            skPoint(sketch, "E96.visualSharp", {"position": v(41.94, -67.98) * mm});
            skArc(sketch, "E96.filletArc", {"start": v(35.6, -67.98) * mm, "mid": v(40.08, -66.12) * mm, "end": v(41.94, -61.63) * mm});
            skLineSegment(sketch, "E97.0", {"start": v(33.56, -65.95) * mm, "end": v(7.4, -65.95) * mm});
            skLineSegment(sketch, "E97.1", {"start": v(39.9, -10.83) * mm, "end": v(39.9, -59.6) * mm});
            skPoint(sketch, "E98.visualSharp", {"position": v(39.9, -65.95) * mm});
            skArc(sketch, "E98.filletArc", {"start": v(33.56, -65.95) * mm, "mid": v(38.05, -64.09) * mm, "end": v(39.9, -59.6) * mm});
            skLineSegment(sketch, "E99", {"start": v(7.4, -65.95) * mm, "end": v(4.62, -67.98) * mm});
            skLineSegment(sketch, "E100", {"start": v(4.62, -67.98) * mm, "end": v(7.4, -67.98) * mm});
            skLineSegment(sketch, "E101", {"start": v(41.94, -10.83) * mm, "end": v(39.9, -10.83) * mm});
            skSolve(sketch);
        }
        {
            var Q0;
            Q0 = qSketchRegion(id + "F39", true);
            extrude(context, id + "F40", {"entities" : qUnion([Q0]), "depth" : 25.4 * mm});
        }
        {
            var Q0;
            Q0=qCreatedBy(makeId("Right.planeOp"),FACE);
            var sketch = newSketch(context, id + "F41", { "sketchPlane" : qUnion([Q0])});
            skLineSegment(sketch, "E102.bottom", {"start": v(85.06, -60.75) * mm, "end": v(21.56, -60.75) * mm});
            skLineSegment(sketch, "E102.top", {"start": v(85.06, -73.45) * mm, "end": v(21.56, -73.45) * mm});
            skLineSegment(sketch, "E102.left", {"start": v(85.06, -60.75) * mm, "end": v(85.06, -73.45) * mm});
            skLineSegment(sketch, "E102.right", {"start": v(21.56, -60.75) * mm, "end": v(21.56, -73.45) * mm});
            skSolve(sketch);
        }
        {
            var Q0;
            Q0 = qSketchRegion(id + "F41", true);
            extrude(context, id + "F42", {"entities" : qUnion([Q0]), "depth" : 1.59 * mm});
        }
        {
            var Q0;
            Q0=makeQuery(id+"F1.opExtrude","CAP_FACE",FACE,{"disambiguationData":[OSD([sQuery(id+"F0.wireOp",EDGE,"E0.bottom"),sQuery(id+"F0.wireOp",EDGE,"E0.top"),sQuery(id+"F0.wireOp",EDGE,"E0.left"),sQuery(id+"F0.wireOp",EDGE,"E0.right"),sQuery(id+"F0.wireOp",EDGE,"E1.bottom"),sQuery(id+"F0.wireOp",EDGE,"E2"),sQuery(id+"F0.wireOp",EDGE,"E3"),sQuery(id+"F0.wireOp",EDGE,"E4.filletArc"),sQuery(id+"F0.wireOp",EDGE,"E5.filletArc")])],"isStart":false});
            var sketch = newSketch(context, id + "F43", { "sketchPlane" : qUnion([Q0])});
            skLineSegment(sketch, "E103.bottom", {"start": v(-41.06, 60.46) * mm, "end": v(-81.2, 60.46) * mm});
            skLineSegment(sketch, "E103.top", {"start": v(-41.06, -53.84) * mm, "end": v(-81.2, -53.84) * mm});
            skLineSegment(sketch, "E103.left", {"start": v(-41.06, 60.46) * mm, "end": v(-41.06, -53.84) * mm});
            skLineSegment(sketch, "E103.right", {"start": v(-81.2, 60.46) * mm, "end": v(-81.2, -53.84) * mm});
            skPoint(sketch, "E103.middle", {"position": v(-61.13, 3.3) * mm});
            skLineSegment(sketch, "E104.bottom", {"start": v(-61.13, -53.84) * mm, "end": v(-47.78, -53.84) * mm});
            skLineSegment(sketch, "E104.top", {"start": v(-61.13, -61.06) * mm, "end": v(-47.78, -61.06) * mm});
            skLineSegment(sketch, "E104.left", {"start": v(-61.13, -53.84) * mm, "end": v(-61.13, -61.06) * mm});
            skLineSegment(sketch, "E104.right", {"start": v(-47.78, -53.84) * mm, "end": v(-47.78, -61.06) * mm});
            skLineSegment(sketch, "E105.bottom", {"start": v(-61.13, 60.46) * mm, "end": v(-46.47, 60.46) * mm});
            skLineSegment(sketch, "E105.top", {"start": v(-61.13, 75.85) * mm, "end": v(-46.47, 75.85) * mm});
            skLineSegment(sketch, "E105.left", {"start": v(-61.13, 60.46) * mm, "end": v(-61.13, 75.85) * mm});
            skLineSegment(sketch, "E105.right", {"start": v(-46.47, 60.46) * mm, "end": v(-46.47, 75.85) * mm});
            skSolve(sketch);
        }
        {
            var Q0;
            {var subQ2=sQuery(id+"F43.wireOp",EDGE,"E104.left");Q0=makeQuery(id+"F43.imprint","IMPRINT",FACE,{"disambiguationData":[TD([[makeQuery(id+"F43.imprint","IMPRINT",EDGE,{"derivedFrom":subQ2}),1.0]])]});}
            var Q1;
            {var subQ2=sQuery(id+"F43.wireOp",EDGE,"E104.right");Q1=makeQuery(id+"F43.imprint","IMPRINT",FACE,{"disambiguationData":[TD([[makeQuery(id+"F43.imprint","IMPRINT",EDGE,{"derivedFrom":subQ2}),-1.0]])]});}
            var Q2;
            {var subQ2=sQuery(id+"F43.wireOp",EDGE,"E105.left");Q2=makeQuery(id+"F43.imprint","IMPRINT",FACE,{"disambiguationData":[TD([[makeQuery(id+"F43.imprint","IMPRINT",EDGE,{"derivedFrom":subQ2}),1.0]])]});}
            var Q3;
            {var subQ2=sQuery(id+"F43.wireOp",EDGE,"E105.right");Q3=makeQuery(id+"F43.imprint","IMPRINT",FACE,{"disambiguationData":[TD([[makeQuery(id+"F43.imprint","IMPRINT",EDGE,{"derivedFrom":subQ2}),1.0]])]});}
            extrude(context, id + "F44", {"entities" : qUnion([Q0, Q1, Q2, Q3]), "operationType" : NewBodyOperationType.REMOVE, "endBound" : BoundingType.THROUGH_ALL, "oppositeDirection" : true, "depth" : 25.4 * mm});
        }
        {
            var Q0;
            {var subQ0=sQuery(id+"F18.wireOp",EDGE,"E60");var subQ1=sQuery(id+"F18.wireOp",EDGE,"E61.top");var subQ2=sQuery(id+"F18.wireOp",EDGE,"E59.1");var subQ3=sQuery(id+"F18.wireOp",EDGE,"E59.0");var subQ4=sQuery(id+"F18.wireOp",EDGE,"E54");var subQ5=sQuery(id+"F18.wireOp",EDGE,"E53");var subQ6=sQuery(id+"F18.wireOp",EDGE,"E59.4");var subQ7=sQuery(id+"F18.wireOp",EDGE,"E61.bottom");var subQ8=sQuery(id+"F18.wireOp",EDGE,"E52");var subQ10=sQuery(id+"F18.wireOp",EDGE,"E51");var subQ12=sQuery(id+"F18.wireOp",EDGE,"E61.left");var subQ13=sQuery(id+"F18.wireOp",EDGE,"E59.2");var subQ14=sQuery(id+"F18.wireOp",EDGE,"E58.0");var subQ15=sQuery(id+"F18.wireOp",EDGE,"E57.0");var subQ16=sQuery(id+"F18.wireOp",EDGE,"E56.0");var subQ17=sQuery(id+"F18.wireOp",EDGE,"E55");var subQ18=sQuery(id+"F18.wireOp",EDGE,"E50.MirrorCS");var subQ19=sQuery(id+"F18.wireOp",EDGE,"E48.top");var subQ20=sQuery(id+"F18.wireOp",EDGE,"E47.left");var subQ21=makeQuery(id+"F30.opExtrude","CAP_FACE",FACE,{"disambiguationData":[OSD([subQ20,subQ19,subQ18,subQ10,subQ8,subQ5,subQ4,subQ17,subQ16,subQ15,subQ14,subQ3,subQ2,subQ13,subQ6,subQ0,subQ7,subQ1,subQ12]),ownerDisambiguation([makeQuery(id+"F30.opExtrude","SWEPT_BODY",BODY,{"disambiguationData":[OSD([sQuery(id+"F29.wireOp",EDGE,"E68.bottom"),sQuery(id+"F29.wireOp",EDGE,"E68.top"),sQuery(id+"F29.wireOp",EDGE,"E68.left"),sQuery(id+"F29.wireOp",EDGE,"E68.right")])]})])],"isStart":false});var subQ22=sQuery(id+"F29.wireOp",EDGE,"E70.left");var subQ24=makeQuery(id+"F19.opExtrude","CAP_FACE",FACE,{"disambiguationData":[OSD([subQ20,subQ19,subQ18,subQ10,subQ8,subQ5,subQ4,subQ17,subQ16,subQ15,subQ14,subQ3,subQ2,subQ13,subQ6,subQ0,subQ7,subQ1,subQ12])],"isStart":false});var subQ32=sQuery(id+"F16.wireOp",EDGE,"E38.left");var subQ34=sQuery(id+"F29.wireOp",EDGE,"E70.right");var subQ35=sQuery(id+"F29.wireOp",EDGE,"E70.top");var subQ36=makeQuery(id+"F30.opExtrude","CAP_FACE",FACE,{"disambiguationData":[OSD([subQ20,subQ19,subQ18,subQ10,subQ8,subQ5,subQ4,subQ17,subQ16,subQ15,subQ14,subQ3,subQ2,subQ13,subQ6,subQ0,subQ7,subQ1,subQ12]),ownerDisambiguation([makeQuery(id+"F30.opExtrude","SWEPT_BODY",BODY,{"disambiguationData":[OSD([sQuery(id+"F29.wireOp",EDGE,"E70.bottom"),subQ35,subQ22,subQ34])]})])],"isStart":false});var subQ37=sQuery(id+"F29.wireOp",EDGE,"E75.MirrorCS");var subQ38=sQuery(id+"F29.wireOp",EDGE,"E74.MirrorCS");var subQ39=sQuery(id+"F29.wireOp",EDGE,"E73.MirrorCS");var subQ40=makeQuery(id+"F30.opExtrude","CAP_FACE",FACE,{"disambiguationData":[OSD([subQ20,subQ19,subQ18,subQ10,subQ8,subQ5,subQ4,subQ17,subQ16,subQ15,subQ14,subQ3,subQ2,subQ13,subQ6,subQ0,subQ7,subQ1,subQ12]),ownerDisambiguation([makeQuery(id+"F30.opExtrude","SWEPT_BODY",BODY,{"disambiguationData":[OSD([sQuery(id+"F29.wireOp",EDGE,"E72.MirrorCS"),subQ39,subQ38,subQ37])]})])],"isStart":false});Q0=makeQuery(id+"F36.boolean.opBoolean","SPLIT",FACE,{"disambiguationData":[TD([makeQuery(id+"F17.opExtrude","SWEPT_FACE",FACE,{"disambiguationData":[OSD([subQ32])]})])],"derivedFrom":makeQuery(id+"F30.boolean.opBoolean","MERGE",FACE,{"derivedFrom":[subQ24,subQ21,subQ36,subQ40]})});}
            var sketch = newSketch(context, id + "F45", { "sketchPlane" : qUnion([Q0])});
            skLineSegment(sketch, "E106.bottom", {"start": v(55.93, 60.1) * mm, "end": v(68.63, 60.1) * mm});
            skLineSegment(sketch, "E106.top", {"start": v(55.93, -54.2) * mm, "end": v(68.63, -54.2) * mm});
            skLineSegment(sketch, "E106.left", {"start": v(55.93, 60.1) * mm, "end": v(55.93, -54.2) * mm});
            skLineSegment(sketch, "E106.right", {"start": v(68.63, 60.1) * mm, "end": v(68.63, -54.2) * mm});
            skSolve(sketch);
        }
        {
            var Q0;
            Q0 = qSketchRegion(id + "F45", true);
            extrude(context, id + "F46", {"entities" : qUnion([Q0]), "operationType" : NewBodyOperationType.REMOVE, "endBound" : BoundingType.THROUGH_ALL, "oppositeDirection" : true, "depth" : 25.4 * mm});
        }
        {
            var Q0;
            Q0=makeQuery(id+"F1.opExtrude","SWEPT_FACE",FACE,{"disambiguationData":[OSD([sQuery(id+"F0.wireOp",EDGE,"E0.left")])]});
            var sketch = newSketch(context, id + "F47", { "sketchPlane" : qUnion([Q0])});
            skLineSegment(sketch, "E107.bottom", {"start": v(-60.46, 30.99) * mm, "end": v(53.84, 30.99) * mm});
            skLineSegment(sketch, "E107.top", {"start": v(-60.46, 22.23) * mm, "end": v(53.84, 22.23) * mm});
            skLineSegment(sketch, "E107.left", {"start": v(-60.46, 30.99) * mm, "end": v(-60.46, 22.23) * mm});
            skLineSegment(sketch, "E107.right", {"start": v(53.84, 30.99) * mm, "end": v(53.84, 22.22) * mm});
            skSolve(sketch);
        }
        {
            var Q0;
            Q0 = qSketchRegion(id + "F47", true);
            extrude(context, id + "F48", {"entities" : qUnion([Q0]), "operationType" : NewBodyOperationType.REMOVE, "endBound" : BoundingType.THROUGH_ALL, "oppositeDirection" : true, "depth" : 25.4 * mm});
        }
        {
            var Q0;
            Q0=qCreatedBy(makeId("Top.planeOp"),FACE);
            var sketch = newSketch(context, id + "F49", { "sketchPlane" : qUnion([Q0])});
            skLineSegment(sketch, "E108.left", {"start": v(-149.85, 61.22) * mm, "end": v(-149.85, -65.78) * mm});
            skLineSegment(sketch, "E109.top", {"start": v(-110.35, 42.17) * mm, "end": v(-65.57, 42.17) * mm});
            skLineSegment(sketch, "E110", {"start": v(-149.85, -2.28) * mm, "end": v(-135.14, -2.28) * mm});
            skLineSegment(sketch, "E111.MirrorCS", {"start": v(-110.35, -46.73) * mm, "end": v(-65.57, -46.73) * mm});
            skLineSegment(sketch, "E112", {"start": v(-149.85, -65.78) * mm, "end": v(-110.35, -65.78) * mm});
            skLineSegment(sketch, "E113", {"start": v(-110.35, -65.78) * mm, "end": v(-110.35, -46.73) * mm});
            skLineSegment(sketch, "E114", {"start": v(-149.85, 61.22) * mm, "end": v(-110.35, 61.22) * mm});
            skLineSegment(sketch, "E115", {"start": v(-110.35, 61.22) * mm, "end": v(-110.35, 42.17) * mm});
            skLineSegment(sketch, "E116", {"start": v(-65.57, 42.17) * mm, "end": v(-65.57, -46.73) * mm});
            skCircle(sketch, "E117", {"center": v(-69.25, 23.43) * mm, "radius": 1.71 * mm});
            skCircle(sketch, "E118.0.1.0", {"center": v(-69.25, -27.37) * mm, "radius": 1.71 * mm});
            skLineSegment(sketch, "E118.direction1", {"start": v(-78.32, 19.92) * mm, "end": v(-53.13, 19.92) * mm, "construction": true});
            skLineSegment(sketch, "E118.direction2", {"start": v(-69.25, 23.43) * mm, "end": v(-69.25, -27.37) * mm, "construction": true});
            skCircle(sketch, "E119", {"center": v(-131.64, -62.66) * mm, "radius": 1.71 * mm});
            skCircle(sketch, "E120.MirrorC", {"center": v(-131.64, 58.1) * mm, "radius": 1.71 * mm});
            skLineSegment(sketch, "E121", {"start": v(-141.57, -65.78) * mm, "end": v(-141.57, -52.21) * mm});
            skLineSegment(sketch, "E122", {"start": v(-141.57, 61.22) * mm, "end": v(-141.57, 47.86) * mm});
            skCircle(sketch, "E123", {"center": v(-141.57, 47.86) * mm, "radius": 1.71 * mm});
            skCircle(sketch, "E124", {"center": v(-141.57, -52.21) * mm, "radius": 1.71 * mm});
            skPoint(sketch, "E125", {"position": v(-69.25, -1.97) * mm});
            skSolve(sketch);
        }
        {
            var Q0;
            Q0 = qSketchRegion(id + "F49", true);
            extrude(context, id + "F50", {"entities" : qUnion([Q0]), "depth" : 1.59 * mm});
        }
        {
            var Q0;
            Q0=makeQuery(id+"F50.opExtrude","CAP_FACE",FACE,{"disambiguationData":[OSD([sQuery(id+"F49.wireOp",EDGE,"E108.left"),sQuery(id+"F49.wireOp",EDGE,"E109.top"),sQuery(id+"F49.wireOp",EDGE,"E111.MirrorCS"),sQuery(id+"F49.wireOp",EDGE,"E112"),sQuery(id+"F49.wireOp",EDGE,"E113"),sQuery(id+"F49.wireOp",EDGE,"E114"),sQuery(id+"F49.wireOp",EDGE,"E115"),sQuery(id+"F49.wireOp",EDGE,"E116"),sQuery(id+"F49.wireOp",EDGE,"E117"),sQuery(id+"F49.wireOp",EDGE,"E118.0.1.0"),sQuery(id+"F49.wireOp",EDGE,"E119"),sQuery(id+"F49.wireOp",EDGE,"E120.MirrorC"),sQuery(id+"F49.wireOp",EDGE,"E123"),sQuery(id+"F49.wireOp",EDGE,"E124")])],"isStart":false});
            var sketch = newSketch(context, id + "F51", { "sketchPlane" : qUnion([Q0])});
            skLineSegment(sketch, "E126.bottom", {"start": v(-143.5, 29.47) * mm, "end": v(-156.2, 29.47) * mm});
            skLineSegment(sketch, "E126.top", {"start": v(-143.5, -34.03) * mm, "end": v(-156.2, -34.03) * mm});
            skLineSegment(sketch, "E126.left", {"start": v(-143.5, 29.47) * mm, "end": v(-143.5, -34.03) * mm});
            skLineSegment(sketch, "E126.right", {"start": v(-156.2, 29.47) * mm, "end": v(-156.2, -34.03) * mm});
            skPoint(sketch, "E126.middle", {"position": v(-149.85, -2.28) * mm});
            skSolve(sketch);
        }
        {
            var Q0;
            Q0 = qSketchRegion(id + "F51", true);
            extrude(context, id + "F52", {"entities" : qUnion([Q0]), "operationType" : NewBodyOperationType.REMOVE, "endBound" : BoundingType.THROUGH_ALL, "oppositeDirection" : true, "depth" : 25.4 * mm});
        }
        {
            var Q0;
            Q0=makeQuery(id+"F19.boolean.opBoolean","MERGE",FACE,{"derivedFrom":[makeQuery(id+"F17.opExtrude","SWEPT_FACE",FACE,{"disambiguationData":[OSD([sQuery(id+"F16.wireOp",EDGE,"E42")])]}),makeQuery(id+"F19.opExtrude","SWEPT_FACE",FACE,{"disambiguationData":[OSD([sQuery(id+"F18.wireOp",EDGE,"E51")])]})]});
            var sketch = newSketch(context, id + "F53", { "sketchPlane" : qUnion([Q0])});
            skLineSegment(sketch, "E127", {"start": v(61, 22.23) * mm, "end": v(61, 0) * mm});
            skCircle(sketch, "E128", {"center": v(61, 15.61) * mm, "radius": 1.7 * mm});
            skCircle(sketch, "E129.0.1.0", {"center": v(61, 6.21) * mm, "radius": 1.7 * mm});
            skLineSegment(sketch, "E129.direction1", {"start": v(61, 15.61) * mm, "end": v(86.61, 15.61) * mm, "construction": true});
            skLineSegment(sketch, "E129.direction2", {"start": v(61, 15.61) * mm, "end": v(61, 6.21) * mm, "construction": true});
            skSolve(sketch);
        }
        {
            var Q0;
            Q0 = qSketchRegion(id + "F53", true);
            extrude(context, id + "F54", {"entities" : qUnion([Q0]), "operationType" : NewBodyOperationType.REMOVE, "endBound" : BoundingType.THROUGH_ALL, "oppositeDirection" : true, "depth" : 25.4 * mm});
        }
        {
            var Q0;
            {var subQ0=sQuery(id+"F18.wireOp",EDGE,"E57.0");var subQ2=sQuery(id+"F18.wireOp",EDGE,"E54");var subQ4=sQuery(id+"F18.wireOp",EDGE,"E53");var subQ6=sQuery(id+"F18.wireOp",EDGE,"E48.top");var subQ9=sQuery(id+"F29.wireOp",EDGE,"E70.left");var subQ11=sQuery(id+"F18.wireOp",EDGE,"E51");var subQ12=sQuery(id+"F18.wireOp",EDGE,"E47.left");var subQ13=sQuery(id+"F18.wireOp",EDGE,"E61.top");var subQ16=sQuery(id+"F29.wireOp",EDGE,"E70.top");var subQ18=sQuery(id+"F18.wireOp",EDGE,"E61.bottom");var subQ21=makeQuery(id+"F17.opExtrude","SWEPT_FACE",FACE,{"disambiguationData":[OSD([sQuery(id+"F16.wireOp",EDGE,"E38.left")])]});var subQ22=makeQuery(id+"F17.opExtrude","SWEPT_FACE",FACE,{"disambiguationData":[OSD([sQuery(id+"F16.wireOp",EDGE,"E39.top")])]});var subQ25=sQuery(id+"F18.wireOp",EDGE,"E59.0");var subQ27=sQuery(id+"F18.wireOp",EDGE,"E59.4");var subQ29=sQuery(id+"F29.wireOp",EDGE,"E70.right");var subQ34=sQuery(id+"F18.wireOp",EDGE,"E61.left");var subQ35=sQuery(id+"F18.wireOp",EDGE,"E60");var subQ36=sQuery(id+"F18.wireOp",EDGE,"E59.2");var subQ37=sQuery(id+"F18.wireOp",EDGE,"E59.1");var subQ38=sQuery(id+"F18.wireOp",EDGE,"E58.0");var subQ39=sQuery(id+"F18.wireOp",EDGE,"E56.0");var subQ40=sQuery(id+"F18.wireOp",EDGE,"E55");var subQ41=sQuery(id+"F18.wireOp",EDGE,"E52");var subQ42=sQuery(id+"F18.wireOp",EDGE,"E50.MirrorCS");var subQ43=makeQuery(id+"F30.opExtrude","CAP_FACE",FACE,{"disambiguationData":[OSD([subQ12,subQ6,subQ42,subQ11,subQ41,subQ4,subQ2,subQ40,subQ39,subQ0,subQ38,subQ25,subQ37,subQ36,subQ27,subQ35,subQ18,subQ13,subQ34]),ownerDisambiguation([makeQuery(id+"F30.opExtrude","SWEPT_BODY",BODY,{"disambiguationData":[OSD([sQuery(id+"F29.wireOp",EDGE,"E70.bottom"),subQ16,subQ9,subQ29])]})])],"isStart":false});var subQ44=makeQuery(id+"F30.opExtrude","CAP_FACE",FACE,{"disambiguationData":[OSD([subQ12,subQ6,subQ42,subQ11,subQ41,subQ4,subQ2,subQ40,subQ39,subQ0,subQ38,subQ25,subQ37,subQ36,subQ27,subQ35,subQ18,subQ13,subQ34]),ownerDisambiguation([makeQuery(id+"F30.opExtrude","SWEPT_BODY",BODY,{"disambiguationData":[OSD([sQuery(id+"F29.wireOp",EDGE,"E68.bottom"),sQuery(id+"F29.wireOp",EDGE,"E68.top"),sQuery(id+"F29.wireOp",EDGE,"E68.left"),sQuery(id+"F29.wireOp",EDGE,"E68.right")])]})])],"isStart":false});var subQ45=makeQuery(id+"F19.opExtrude","CAP_FACE",FACE,{"disambiguationData":[OSD([subQ12,subQ6,subQ42,subQ11,subQ41,subQ4,subQ2,subQ40,subQ39,subQ0,subQ38,subQ25,subQ37,subQ36,subQ27,subQ35,subQ18,subQ13,subQ34])],"isStart":false});var subQ46=sQuery(id+"F29.wireOp",EDGE,"E75.MirrorCS");var subQ47=sQuery(id+"F29.wireOp",EDGE,"E74.MirrorCS");var subQ48=sQuery(id+"F29.wireOp",EDGE,"E73.MirrorCS");var subQ49=makeQuery(id+"F30.opExtrude","CAP_FACE",FACE,{"disambiguationData":[OSD([subQ12,subQ6,subQ42,subQ11,subQ41,subQ4,subQ2,subQ40,subQ39,subQ0,subQ38,subQ25,subQ37,subQ36,subQ27,subQ35,subQ18,subQ13,subQ34]),ownerDisambiguation([makeQuery(id+"F30.opExtrude","SWEPT_BODY",BODY,{"disambiguationData":[OSD([sQuery(id+"F29.wireOp",EDGE,"E72.MirrorCS"),subQ48,subQ47,subQ46])]})])],"isStart":false});Q0=makeQuery(id+"F46.boolean.opBoolean","SPLIT",FACE,{"disambiguationData":[TD([subQ22])],"derivedFrom":makeQuery(id+"F36.boolean.opBoolean","SPLIT",FACE,{"disambiguationData":[TD([subQ21])],"derivedFrom":makeQuery(id+"F30.boolean.opBoolean","MERGE",FACE,{"derivedFrom":[subQ45,subQ44,subQ43,subQ49]})})});}
            var sketch = newSketch(context, id + "F55", { "sketchPlane" : qUnion([Q0])});
            skLineSegment(sketch, "E130.left", {"start": v(55.93, 66.4) * mm, "end": v(55.93, -60.6) * mm});
            skLineSegment(sketch, "E131.top", {"start": v(95.44, 47.35) * mm, "end": v(140.19, 47.35) * mm});
            skLineSegment(sketch, "E132", {"start": v(55.93, 2.9) * mm, "end": v(70.8, 2.9) * mm});
            skLineSegment(sketch, "E133.MirrorCS", {"start": v(95.44, -41.55) * mm, "end": v(140.19, -41.55) * mm});
            skLineSegment(sketch, "E134", {"start": v(55.93, -60.6) * mm, "end": v(95.44, -60.6) * mm});
            skLineSegment(sketch, "E135", {"start": v(95.44, -60.6) * mm, "end": v(95.44, -41.55) * mm});
            skLineSegment(sketch, "E136", {"start": v(55.93, 66.4) * mm, "end": v(95.44, 66.4) * mm});
            skLineSegment(sketch, "E137", {"start": v(95.44, 66.4) * mm, "end": v(95.44, 47.35) * mm});
            skLineSegment(sketch, "E138", {"start": v(140.19, 47.35) * mm, "end": v(140.19, -41.55) * mm});
            skCircle(sketch, "E139", {"center": v(136.5, 28.61) * mm, "radius": 1.71 * mm});
            skCircle(sketch, "E140.0.1.0", {"center": v(136.5, -22.19) * mm, "radius": 1.71 * mm});
            skLineSegment(sketch, "E140.direction2", {"start": v(136.5, 28.61) * mm, "end": v(136.5, -22.19) * mm, "construction": true});
            skCircle(sketch, "E141", {"center": v(74.14, -57.48) * mm, "radius": 1.71 * mm});
            skCircle(sketch, "E142.MirrorC", {"center": v(74.14, 63.28) * mm, "radius": 1.71 * mm});
            skLineSegment(sketch, "E143", {"start": v(62.08, -60.6) * mm, "end": v(62.08, -47.03) * mm});
            skLineSegment(sketch, "E144", {"start": v(62.08, 66.4) * mm, "end": v(62.08, 53.05) * mm});
            skCircle(sketch, "E145", {"center": v(62.08, 53.05) * mm, "radius": 1.71 * mm});
            skCircle(sketch, "E146", {"center": v(62.08, -47.03) * mm, "radius": 1.71 * mm});
            skSolve(sketch);
        }
        {
            var Q0;
            {var subQ0=sQuery(id+"F55.wireOp",EDGE,"E137");var subQ1=sQuery(id+"F55.wireOp",EDGE,"E136");var subQ2=makeQuery(id+"F55.imprint","INTERSECT",VERTEX,{"derivedFrom":[subQ1,subQ0]});Q0=makeQuery(id+"F55.imprint","IMPRINT",FACE,{"disambiguationData":[TD([[makeQuery(id+"F55.imprint","IMPRINT",EDGE,{"disambiguationData":[TD([[subQ2,1.0]])],"derivedFrom":subQ1}),-1.0]])]});}
            var Q1;
            Q1=makeQuery(id+"F55.imprint","IMPRINT",FACE,{"disambiguationData":[TD([[makeQuery(id+"F55.imprint","IMPRINT",EDGE,{"derivedFrom":sQuery(id+"F55.wireOp",EDGE,"E142.MirrorC")}),-1.0]])]});
            var Q2;
            Q2=makeQuery(id+"F55.imprint","IMPRINT",FACE,{"disambiguationData":[TD([[makeQuery(id+"F55.imprint","IMPRINT",EDGE,{"derivedFrom":sQuery(id+"F55.wireOp",EDGE,"E139")}),1.0]])]});
            var Q3;
            Q3=makeQuery(id+"F55.imprint","IMPRINT",FACE,{"disambiguationData":[TD([[makeQuery(id+"F55.imprint","IMPRINT",EDGE,{"derivedFrom":sQuery(id+"F55.wireOp",EDGE,"E140.0.1.0")}),1.0]])]});
            var Q4;
            Q4=makeQuery(id+"F55.imprint","IMPRINT",FACE,{"disambiguationData":[TD([[makeQuery(id+"F55.imprint","IMPRINT",EDGE,{"derivedFrom":sQuery(id+"F55.wireOp",EDGE,"E141")}),1.0]])]});
            var Q5;
            Q5=sQuery(id+"F55.wireOp",EDGE,"E138");
            var Q6;
            Q6=sQuery(id+"F55.wireOp",EDGE,"E130.left");
            var Q7;
            Q7=sQuery(id+"F55.wireOp",EDGE,"E143");
            var Q8;
            Q8=sQuery(id+"F55.wireOp",EDGE,"E137");
            var Q9;
            Q9=sQuery(id+"F55.wireOp",EDGE,"E135");
            var Q10;
            Q10=sQuery(id+"F55.wireOp",EDGE,"E136");
            var Q11;
            Q11=sQuery(id+"F55.wireOp",EDGE,"E134");
            var Q12;
            Q12=sQuery(id+"F55.wireOp",EDGE,"E131.top");
            var Q13;
            Q13=sQuery(id+"F55.wireOp",EDGE,"E132");
            var Q14;
            Q14=sQuery(id+"F55.wireOp",EDGE,"E144");
            var Q15;
            Q15=sQuery(id+"F55.wireOp",EDGE,"E142.MirrorC");
            var Q16;
            Q16=sQuery(id+"F55.wireOp",EDGE,"E141");
            var Q17;
            Q17=sQuery(id+"F55.wireOp",EDGE,"E139");
            var Q18;
            Q18=sQuery(id+"F55.wireOp",EDGE,"E146");
            var Q19;
            Q19=sQuery(id+"F55.wireOp",EDGE,"E145");
            var Q20;
            Q20=sQuery(id+"F55.wireOp",EDGE,"E140.0.1.0");
            var Q21;
            Q21=sQuery(id+"F55.wireOp",EDGE,"E133.MirrorCS");
            extrude(context, id + "F56", {"entities" : qUnion([Q0, Q1, Q2, Q3, Q4]), "operationType" : NewBodyOperationType.REMOVE, "surfaceEntities" : qUnion([Q5, Q6, Q7, Q8, Q9, Q10, Q11, Q12, Q13, Q14, Q15, Q16, Q17, Q18, Q19, Q20, Q21]), "oppositeDirection" : true, "depth" : 9.52 * mm});
        }
    });
